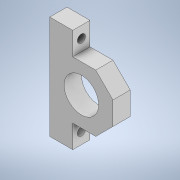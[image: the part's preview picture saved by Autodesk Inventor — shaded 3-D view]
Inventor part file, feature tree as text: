
AUTODESK INVENTOR PART (.ipt)
format: ipt  version: 2022 (Build 260153000, 153)  size: 133,632 bytes
history: native  units: mm
features: extrude x2, sketch x2, other x1
ambient origin geometry x8: Origin, YZ Plane, XZ Plane, XY Plane, X Axis, Y Axis, Z Axis, Center Point
bodies: Body1 (feature_tree)
feature tree (5):
  other  "Sólido1"
  extrude  "Extrusión1"  Depth=15.0mm
  extrude  "Extrusión4"  Depth=20.0mm TaperAngle=0.0deg
  sketch  "Boceto1"  dims[d0=20.0mm d1=20.0mm d2=20.0mm d3=90.0mm d4=20.0mm d5=20.0mm d6=55.0mm d7=30.0mm d8=15.0mm d9=0.0mm d19=7.0mm]
  sketch  "Boceto4"  dims[d20=7.0mm d21=20.0mm d22=0.0mm d23=0.5mm d24=0.872665mm]
